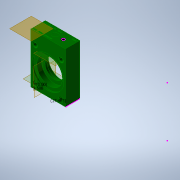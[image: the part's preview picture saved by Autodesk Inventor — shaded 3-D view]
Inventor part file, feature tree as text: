
AUTODESK INVENTOR PART (.ipt)
format: ipt  version: 2020 (Build 240168000, 168)  size: 769,024 bytes
history: native  units: in
note: dims shown in document units (in); Inventor stores cm internally (conversion verified against a paired STEP export)
features: plane x7, sketch x6, hole x4, extrude x3
ambient origin geometry x8: Origin, YZ Plane, XZ Plane, XY Plane, X Axis, Y Axis, Z Axis, Center Point
bodies: Solid1 (feature_tree), Solid2 (feature_tree)
feature tree (20):
  plane  "Work Plane1"
  extrude  "Extrusion1"  Depth=0.3937in TaperAngle=0.0deg
  plane  "Work Plane3"
  extrude  "Extrusion2"  Depth=0.375in
  plane  "Work Plane6"
  sketch  "Sketch3"  dims[d11=0.213in d12=0.2362in d13=0.4375in d14=0.25in d15=0.563in d16=0.375in d17=0.0in d18=0.3743in]
  hole  "Hole1"  [1 undecoded]
  hole  "Hole2"  [1 undecoded]
  plane  "Work Plane2"
  plane  "Work Plane5"
  sketch  "Sketch6"  dims[d36=0.6875in]
  plane  "Work Plane4"
  extrude  "Extrusion3"  [1 undecoded]
  hole  "Hole5"  [1 undecoded]
  plane  "Work Plane7"
  hole  "Hole6"  [1 undecoded]
  sketch  "Sketch1"  dims[d0=0.6398in d1=0.0in d2=0.3937in d3=0.0in]
  sketch  "Sketch2"  dims[d4=0.04in d5=0.2362in d6=0.4375in d7=0.25in d8=0.563in d9=0.9843in d10=0.8108in]
  sketch  "Sketch5"  dims[d19=0.0in d34=0.1181in d35=0.0in]
  sketch  "Sketch8"  dims[d37=0.213in d38=0.2362in d39=0.1575in d40=0.0787in d41=90.0deg d42=0.25in d43=0.0in d44=0.04in d45=0.2362in d46=0.1575in d47=0.0787in d48=90.0deg d49=0.4724in d50=0.481in d51=0.2701in]
note: 5 required parameter values undecoded (feature->parameter linkage not recoverable at this tier; creation-order binding heuristic only, values carry confidence <= 0.55)
